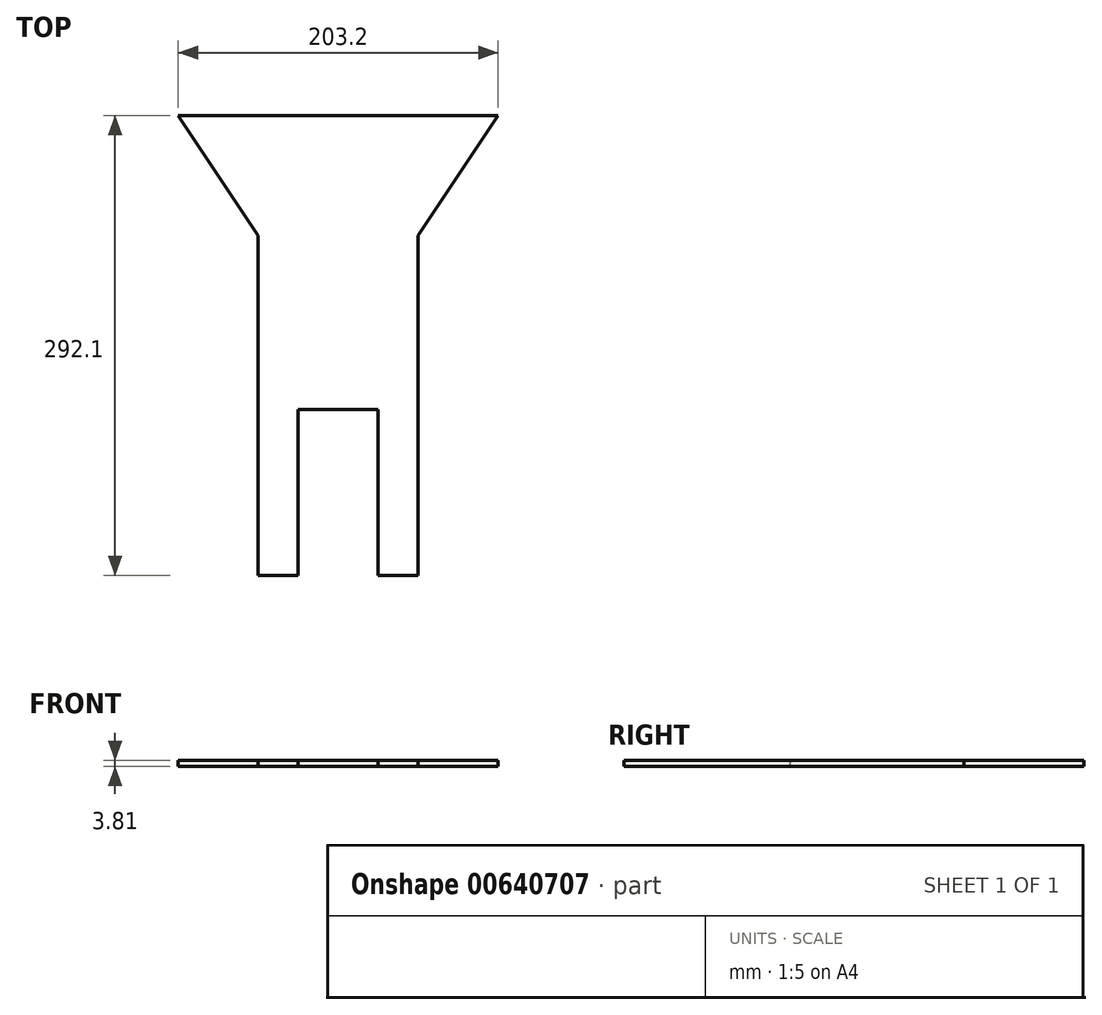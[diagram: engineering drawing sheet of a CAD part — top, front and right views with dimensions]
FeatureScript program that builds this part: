
annotation { "Feature Type Name" : "Feature", "Feature Type Description" : "" }
export const myFeature = defineFeature(function(context is Context, id is Id, definition is map)
    precondition{}
    {
        {
            var Q0;
            Q0=qCreatedBy(makeId("Top.planeOp"),FACE);
            var sketch = newSketch(context, id + "F0", { "sketchPlane" : qUnion([Q0])});
            skLineSegment(sketch, "E0", {"start": v(0, 0) * mm, "end": v(-25.4, 0) * mm});
            skLineSegment(sketch, "E1", {"start": v(-25.4, 0) * mm, "end": v(-25.4, 105.41) * mm});
            skLineSegment(sketch, "E2", {"start": v(-25.4, 105.41) * mm, "end": v(-76.2, 105.41) * mm});
            skLineSegment(sketch, "E3", {"start": v(-76.2, 105.41) * mm, "end": v(-76.2, 0) * mm});
            skLineSegment(sketch, "E4", {"start": v(-76.2, 0) * mm, "end": v(-101.6, 0) * mm});
            skLineSegment(sketch, "E5", {"start": v(-101.6, 0) * mm, "end": v(-101.6, 215.9) * mm});
            skLineSegment(sketch, "E6", {"start": v(-152.4, 292.1) * mm, "end": v(-101.6, 215.9) * mm});
            skLineSegment(sketch, "E7.MirrorCS", {"start": v(50.8, 292.1) * mm, "end": v(0, 215.9) * mm});
            skLineSegment(sketch, "E8.MirrorCS", {"start": v(0, 0) * mm, "end": v(0, 215.9) * mm});
            skPoint(sketch, "E9.start.orphan", {"position": v(-50.8, 105.41) * mm});
            skLineSegment(sketch, "E10", {"start": v(-152.4, 292.1) * mm, "end": v(50.8, 292.1) * mm});
            skSolve(sketch);
        }
        {
            var Q0;
            Q0=makeQuery(id+"F0.imprint","IMPRINT",FACE,{"disambiguationData":[TD([[makeQuery(id+"F0.imprint","IMPRINT",EDGE,{"derivedFrom":sQuery(id+"F0.wireOp",EDGE,"E0")}),-1.0]])]});
            extrude(context, id + "F1", {"entities" : qUnion([Q0]), "depth" : 3.8 * mm, "offsetDistance" : 25.4 * mm});
        }
    });
